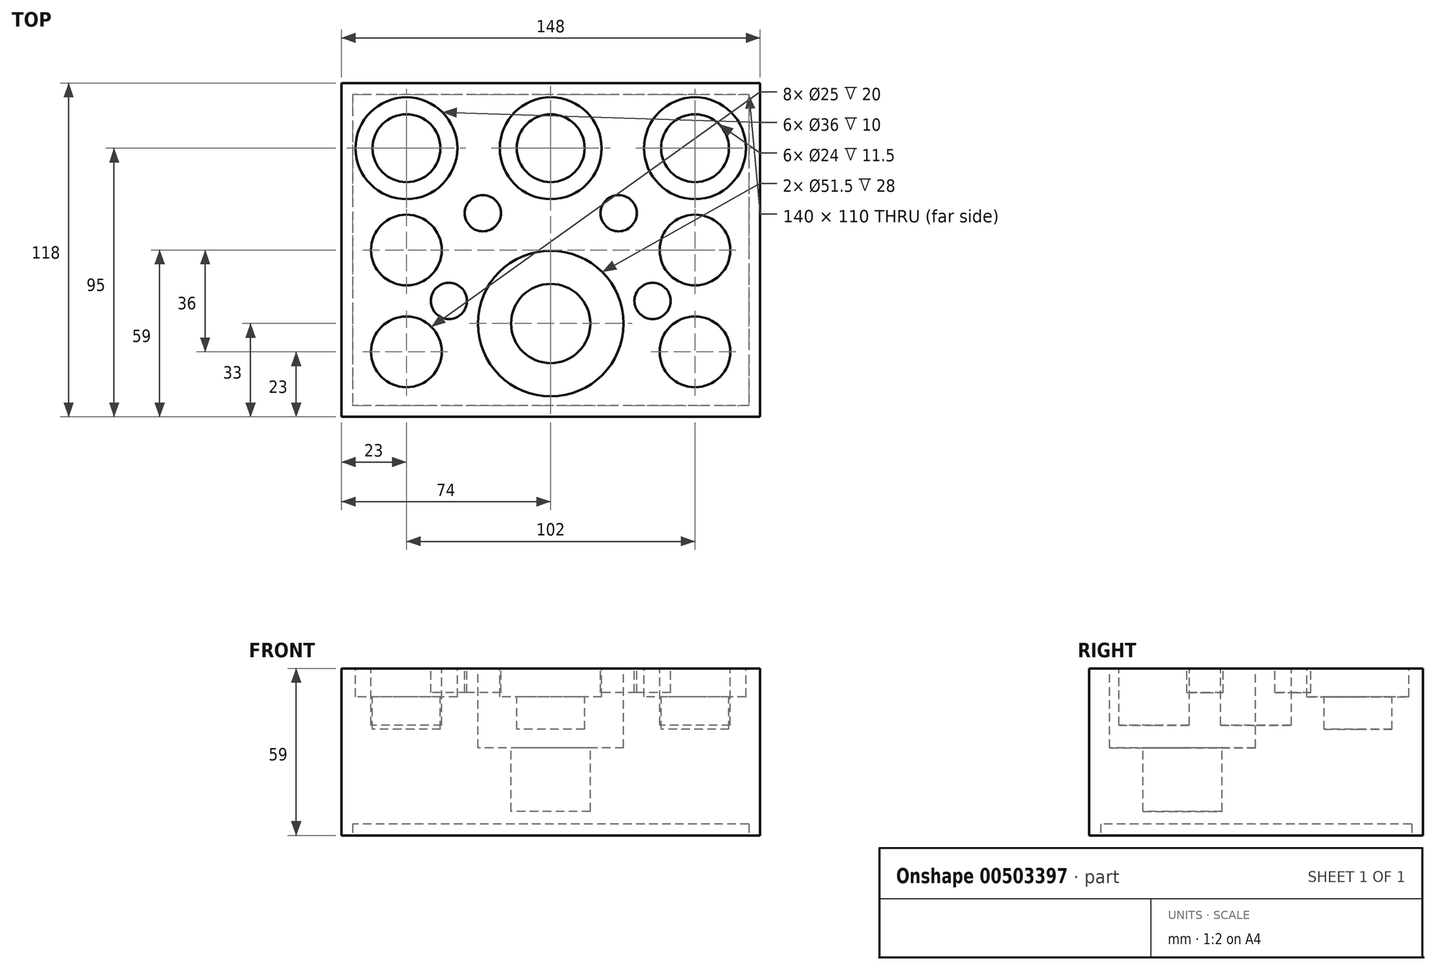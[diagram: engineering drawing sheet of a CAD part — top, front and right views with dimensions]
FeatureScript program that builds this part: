
annotation { "Feature Type Name" : "Feature", "Feature Type Description" : "" }
export const myFeature = defineFeature(function(context is Context, id is Id, definition is map)
    precondition{}
    {
        {
            var Q0;
            Q0=qCreatedBy(makeId("Top.planeOp"),FACE);
            var sketch = newSketch(context, id + "F0", { "sketchPlane" : qUnion([Q0])});
            skLineSegment(sketch, "E0.bottom", {"start": v(74, -59) * mm, "end": v(-74, -59) * mm});
            skLineSegment(sketch, "E0.top", {"start": v(74, 59) * mm, "end": v(-74, 59) * mm});
            skLineSegment(sketch, "E0.left", {"start": v(74, -59) * mm, "end": v(74, 59) * mm});
            skLineSegment(sketch, "E0.right", {"start": v(-74, -59) * mm, "end": v(-74, 59) * mm});
            skPoint(sketch, "E0.middle", {"position": v(0, 0) * mm});
            skSolve(sketch);
        }
        {
            var Q0;
            Q0=qSketchRegion(id+"F0",true);
            extrude(context, id + "F1", {"entities" : qUnion([Q0]), "depth" : 59 * mm, "offsetDistance" : 25 * mm});
        }
        {
            var Q0;
            Q0=makeQuery(id+"F1.opExtrude","CAP_FACE",FACE,{"disambiguationData":[OSD([sQuery(id+"F0.wireOp",EDGE,"E0.bottom"),sQuery(id+"F0.wireOp",EDGE,"E0.top"),sQuery(id+"F0.wireOp",EDGE,"E0.left"),sQuery(id+"F0.wireOp",EDGE,"E0.right")])],"isStart":false});
            var sketch = newSketch(context, id + "F2", { "sketchPlane" : qUnion([Q0])});
            skPoint(sketch, "E1.middle", {"position": v(0, 0) * mm});
            skCircle(sketch, "E2", {"center": v(-51, 36) * mm, "radius": 18 * mm});
            skCircle(sketch, "E3", {"center": v(51, 36) * mm, "radius": 18 * mm});
            skCircle(sketch, "E4", {"center": v(51, -36) * mm, "radius": 12.5 * mm});
            skCircle(sketch, "E5", {"center": v(-51, -36) * mm, "radius": 12.5 * mm});
            skCircle(sketch, "E6", {"center": v(-51, 0) * mm, "radius": 12.5 * mm});
            skCircle(sketch, "E7", {"center": v(51, 0) * mm, "radius": 12.5 * mm});
            skCircle(sketch, "E8", {"center": v(0, 36) * mm, "radius": 18 * mm});
            skCircle(sketch, "E9", {"center": v(-36, -18) * mm, "radius": 6.4 * mm});
            skCircle(sketch, "E10", {"center": v(-24, 13) * mm, "radius": 6.4 * mm});
            skCircle(sketch, "E11", {"center": v(24, 13) * mm, "radius": 6.4 * mm});
            skCircle(sketch, "E12", {"center": v(36, -18) * mm, "radius": 6.4 * mm});
            skCircle(sketch, "E13", {"center": v(0, -26) * mm, "radius": 25.75 * mm});
            skCircle(sketch, "E14", {"center": v(0, -26) * mm, "radius": 14 * mm});
            skCircle(sketch, "E15", {"center": v(0, 36) * mm, "radius": 12 * mm});
            skCircle(sketch, "E16", {"center": v(51, 36) * mm, "radius": 12 * mm});
            skCircle(sketch, "E17", {"center": v(-51, 36) * mm, "radius": 12 * mm});
            skSolve(sketch);
        }
        {
            var Q0;
            Q0=makeQuery(id+"F2.imprint","IMPRINT",FACE,{"disambiguationData":[TD([[makeQuery(id+"F2.imprint","IMPRINT",EDGE,{"derivedFrom":sQuery(id+"F2.wireOp",EDGE,"E14")}),1.0]])]});
            extrude(context, id + "F3", {"entities" : qUnion([Q0]), "operationType" : NewBodyOperationType.REMOVE, "oppositeDirection" : true, "depth" : 50.5 * mm, "offsetDistance" : 25 * mm});
        }
        {
            var Q0;
            Q0=makeQuery(id+"F2.imprint","IMPRINT",FACE,{"disambiguationData":[TD([[makeQuery(id+"F2.imprint","IMPRINT",EDGE,{"derivedFrom":sQuery(id+"F2.wireOp",EDGE,"E13")}),1.0]])]});
            extrude(context, id + "F4", {"entities" : qUnion([Q0]), "operationType" : NewBodyOperationType.REMOVE, "oppositeDirection" : true, "depth" : 28 * mm, "offsetDistance" : 25 * mm});
        }
        {
            var Q0;
            Q0=makeQuery(id+"F2.imprint","IMPRINT",FACE,{"disambiguationData":[TD([[makeQuery(id+"F2.imprint","IMPRINT",EDGE,{"derivedFrom":sQuery(id+"F2.wireOp",EDGE,"E17")}),1.0]])]});
            var Q1;
            Q1=makeQuery(id+"F2.imprint","IMPRINT",FACE,{"disambiguationData":[TD([[makeQuery(id+"F2.imprint","IMPRINT",EDGE,{"derivedFrom":sQuery(id+"F2.wireOp",EDGE,"E15")}),1.0]])]});
            var Q2;
            Q2=makeQuery(id+"F2.imprint","IMPRINT",FACE,{"disambiguationData":[TD([[makeQuery(id+"F2.imprint","IMPRINT",EDGE,{"derivedFrom":sQuery(id+"F2.wireOp",EDGE,"E16")}),1.0]])]});
            extrude(context, id + "F5", {"entities" : qUnion([Q0, Q1, Q2]), "operationType" : NewBodyOperationType.REMOVE, "oppositeDirection" : true, "depth" : 21.5 * mm, "offsetDistance" : 25 * mm});
        }
        {
            var Q0;
            Q0=makeQuery(id+"F2.imprint","IMPRINT",FACE,{"disambiguationData":[TD([[makeQuery(id+"F2.imprint","IMPRINT",EDGE,{"derivedFrom":sQuery(id+"F2.wireOp",EDGE,"E2")}),1.0]])]});
            var Q1;
            Q1=makeQuery(id+"F2.imprint","IMPRINT",FACE,{"disambiguationData":[TD([[makeQuery(id+"F2.imprint","IMPRINT",EDGE,{"derivedFrom":sQuery(id+"F2.wireOp",EDGE,"E8")}),1.0]])]});
            var Q2;
            Q2=makeQuery(id+"F2.imprint","IMPRINT",FACE,{"disambiguationData":[TD([[makeQuery(id+"F2.imprint","IMPRINT",EDGE,{"derivedFrom":sQuery(id+"F2.wireOp",EDGE,"E3")}),1.0]])]});
            extrude(context, id + "F6", {"entities" : qUnion([Q0, Q1, Q2]), "operationType" : NewBodyOperationType.REMOVE, "oppositeDirection" : true, "depth" : 10 * mm, "offsetDistance" : 25 * mm});
        }
        {
            var Q0;
            Q0=makeQuery(id+"F2.imprint","IMPRINT",FACE,{"disambiguationData":[TD([[makeQuery(id+"F2.imprint","IMPRINT",EDGE,{"derivedFrom":sQuery(id+"F2.wireOp",EDGE,"E9")}),1.0]])]});
            var Q1;
            Q1=makeQuery(id+"F2.imprint","IMPRINT",FACE,{"disambiguationData":[TD([[makeQuery(id+"F2.imprint","IMPRINT",EDGE,{"derivedFrom":sQuery(id+"F2.wireOp",EDGE,"E10")}),1.0]])]});
            var Q2;
            Q2=makeQuery(id+"F2.imprint","IMPRINT",FACE,{"disambiguationData":[TD([[makeQuery(id+"F2.imprint","IMPRINT",EDGE,{"derivedFrom":sQuery(id+"F2.wireOp",EDGE,"E11")}),1.0]])]});
            var Q3;
            Q3=makeQuery(id+"F2.imprint","IMPRINT",FACE,{"disambiguationData":[TD([[makeQuery(id+"F2.imprint","IMPRINT",EDGE,{"derivedFrom":sQuery(id+"F2.wireOp",EDGE,"E12")}),1.0]])]});
            extrude(context, id + "F7", {"entities" : qUnion([Q0, Q1, Q2, Q3]), "operationType" : NewBodyOperationType.REMOVE, "oppositeDirection" : true, "depth" : 8.5 * mm, "offsetDistance" : 25 * mm});
        }
        {
            var Q0;
            Q0=makeQuery(id+"F2.imprint","IMPRINT",FACE,{"disambiguationData":[TD([[makeQuery(id+"F2.imprint","IMPRINT",EDGE,{"derivedFrom":sQuery(id+"F2.wireOp",EDGE,"E5")}),1.0]])]});
            var Q1;
            Q1=makeQuery(id+"F2.imprint","IMPRINT",FACE,{"disambiguationData":[TD([[makeQuery(id+"F2.imprint","IMPRINT",EDGE,{"derivedFrom":sQuery(id+"F2.wireOp",EDGE,"E6")}),1.0]])]});
            var Q2;
            Q2=makeQuery(id+"F2.imprint","IMPRINT",FACE,{"disambiguationData":[TD([[makeQuery(id+"F2.imprint","IMPRINT",EDGE,{"derivedFrom":sQuery(id+"F2.wireOp",EDGE,"E7")}),1.0]])]});
            var Q3;
            Q3=makeQuery(id+"F2.imprint","IMPRINT",FACE,{"disambiguationData":[TD([[makeQuery(id+"F2.imprint","IMPRINT",EDGE,{"derivedFrom":sQuery(id+"F2.wireOp",EDGE,"E4")}),1.0]])]});
            extrude(context, id + "F8", {"entities" : qUnion([Q0, Q1, Q2, Q3]), "operationType" : NewBodyOperationType.REMOVE, "oppositeDirection" : true, "depth" : 20 * mm, "offsetDistance" : 25 * mm});
        }
        {
            var Q0;
            Q0=makeQuery(id+"F0.imprint","IMPRINT",FACE,{"disambiguationData":[TD([[makeQuery(id+"F0.imprint","IMPRINT",EDGE,{"derivedFrom":sQuery(id+"F0.wireOp",EDGE,"E0.bottom")}),-1.0]])]});
            var sketch = newSketch(context, id + "F9", { "sketchPlane" : qUnion([Q0])});
            skLineSegment(sketch, "E18.bottom", {"start": v(70, 55) * mm, "end": v(-70, 55) * mm});
            skLineSegment(sketch, "E18.top", {"start": v(70, -55) * mm, "end": v(-70, -55) * mm});
            skLineSegment(sketch, "E18.left", {"start": v(70, 55) * mm, "end": v(70, -55) * mm});
            skLineSegment(sketch, "E18.right", {"start": v(-70, 55) * mm, "end": v(-70, -55) * mm});
            skPoint(sketch, "E18.middle", {"position": v(0, 0) * mm});
            skSolve(sketch);
        }
        {
            var Q0;
            Q0=makeQuery(id+"F9.imprint","IMPRINT",FACE,{"disambiguationData":[TD([[makeQuery(id+"F9.imprint","IMPRINT",EDGE,{"derivedFrom":sQuery(id+"F9.wireOp",EDGE,"E18.bottom")}),1.0]])]});
            extrude(context, id + "F10", {"entities" : qUnion([Q0]), "operationType" : NewBodyOperationType.REMOVE, "depth" : 4 * mm, "offsetDistance" : 25 * mm});
        }
    });
